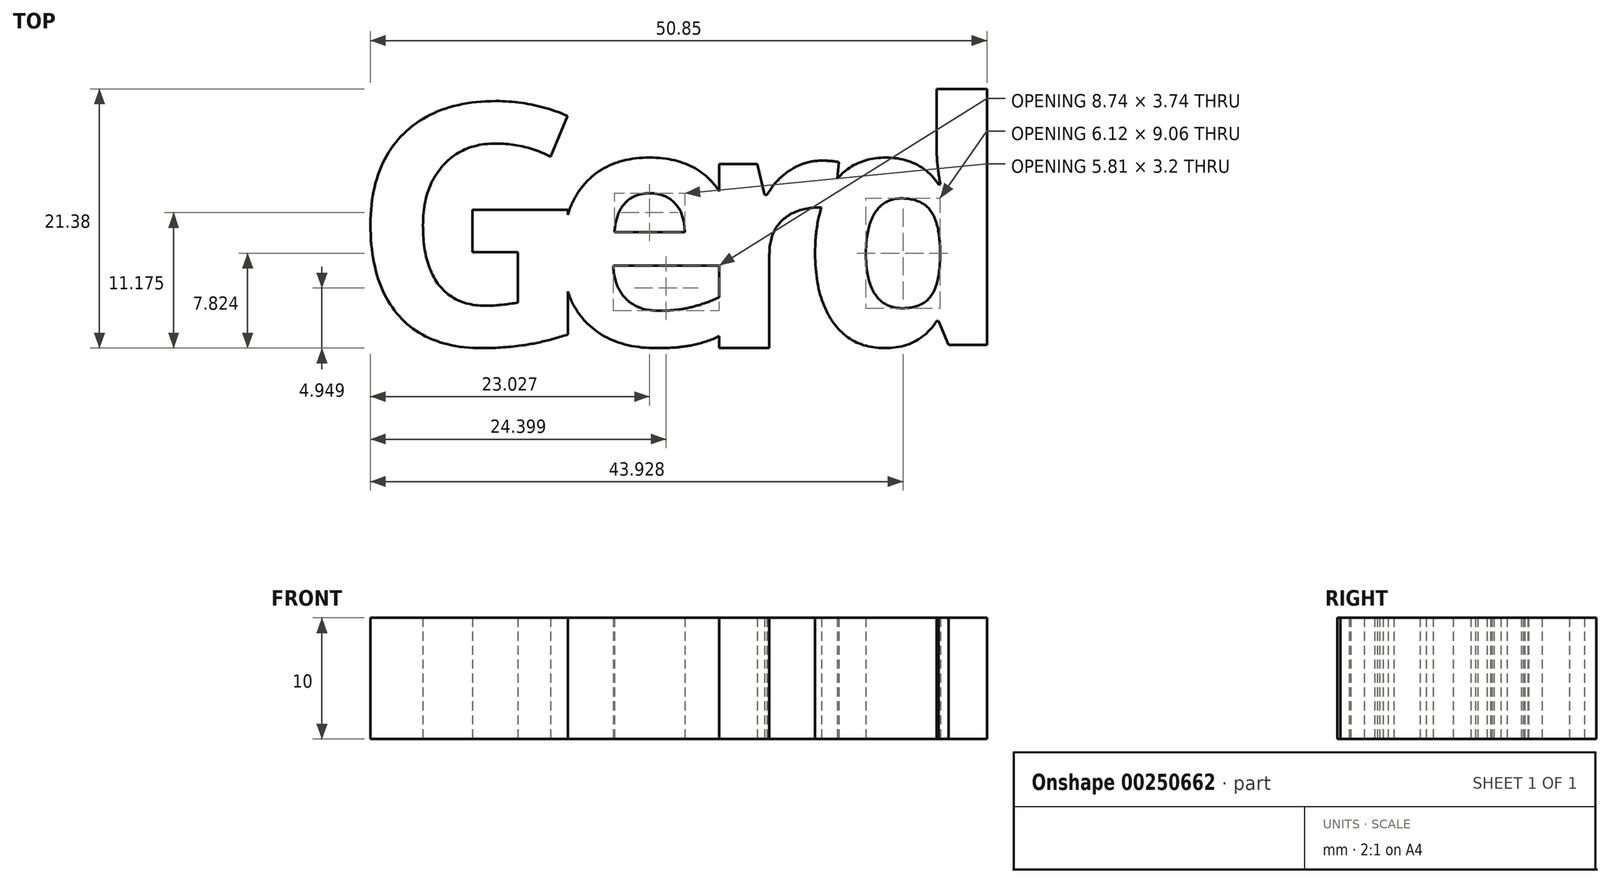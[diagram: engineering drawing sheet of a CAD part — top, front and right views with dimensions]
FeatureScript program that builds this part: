
annotation { "Feature Type Name" : "Feature", "Feature Type Description" : "" }
export const myFeature = defineFeature(function(context is Context, id is Id, definition is map)
    precondition{}
    {
        {
            var Q0;
            Q0=qCreatedBy(makeId("Top.planeOp"), FACE);
            var sketch = newSketch(context, id + "F0", { "sketchPlane" : qUnion([Q0])});
            skText(sketch, "E0", { "text": "G", "fontName": "OpenSans-Bold.ttf"});
            skText(sketch, "E1", { "text": "e", "fontName": "OpenSans-Bold.ttf"});
            skText(sketch, "E2", { "text": "r", "fontName": "OpenSans-Bold.ttf"});
            skText(sketch, "E3", { "text": "d", "fontName": "OpenSans-Bold.ttf"});
            const initialGuessF0  = {"E0": [0, 0, 1, 0, 0.02], "E1": [0.0162, 0, 1, 0, 0.02], "E2": [0.02821, -0.00025, 1, 0, 0.02], "E3": [0.03704, 0, 1, 0, 0.02]};
            skSetInitialGuess(sketch, initialGuessF0);
            skSolve(sketch);
        }
        {
            var Q0;
            Q0 = qSketchRegion(id + "F0", true);
            extrude(context, id + "F1", {"entities" : qUnion([Q0]), "depth" : 10 * mm, "offsetDistance" : 25 * mm});
        }
    });
